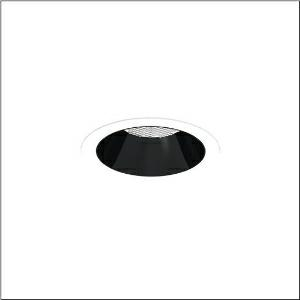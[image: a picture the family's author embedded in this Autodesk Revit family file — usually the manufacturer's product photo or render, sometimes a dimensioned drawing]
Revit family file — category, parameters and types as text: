
# Revit family: lunis_21_l_51db17ed91c
name_source: partatom
category: Lighting Fixtures
units: mm (PartAtom-declared; Revit-internal decimal feet)

## family parameters
Cut with Voids When Loaded = No
Host = Face
Light Source = No
Part Type = Normal
Room Calculation Point = No
Round Connector Dimension = Use Diameter
Shared = No

## types (1)
- --- (1 x LED, 3430 lm, 25.4 W, 6500K)
    Apparent Load = 25 VA
    CIE Flux Codes = 93 100 100 100 100
    Color Rendering = 80
    Color Temperature = 6500K
    Default Elevation = 1800 mm
    Description = Lunis 21 L, downlight, light control with lens, of PMMA, anti glare with reflector, of PC, light emission: direct distribution, LED rated luminous flux: 1.790lm, light colour: 830/840/865, with terminal, 5-pole, mains connection: 220..240V, AC/DC, 0/50..60Hz, housing, round, of diecast aluminium, traffic white (RAL 9016), diameter: 165mm, clamping range: 1..40mm, protection rating (complete): IP20, protection rating (on room side): IP54, insulation class (complete): insulation class II (safety insulation), certification: CE, impact resistance: IK03, packaging unit: 1 piece
    Height = 0 mm  [stored 0 ft]
    Lamp = 1 x LED
    Lamp Light Flux = 3430 lm
    Lamp Power = 25.4 W
    Lamp count = 1
    Length = 165 mm
    Luminous efficacy = 135 lm/W
    Manufacturer = Siteco
    ModVariant = No
    Model = 51DB17ED91C
    Mounting Place = Ceiling
    Mounting Type = Recessed
    Number of Poles = 1
    OnlyDefault = Yes
    Power Factor = 1
    Product Name = Lunis 21 L
    Product group = downlight
    ProductGroupID = 401
    Protection Class = Protection class II
    Protection Degree = IP 20
    RLX_Detail_Level = 1
    RLX_Emergency_Light_Flux = 0 lm
    RLX_Emergency_Type = 0
    RLX_Emergency_Type_DB = No
    RlxData = <blob elided: 18525 chars, md5=04857bc7>
    Socket = socket
    Standby Power = 0 W
    System Light Flux = 3430 lm
    System Power = 25 W
    Type Comments = individual setting: colour temperature 6500K, luminous flux: 100 % | (ON | ON | OFF | OFF) | 700 mA
    Type Image = l_1291094.jpg
    URL = http://relux.com
    VarID = @adj_035757
    Voltage = 0 V
    Weight = 0.00 kg
    Width = 0 mm  [stored 0 ft]

note: [stored X ft] marks values corroborated as IEEE doubles in the binary element streams (Revit-internal decimal feet)

## geometry (parser evidence)
native form markers: Blend x4, Sweep x10
no freeform markers — native parametric forms only
